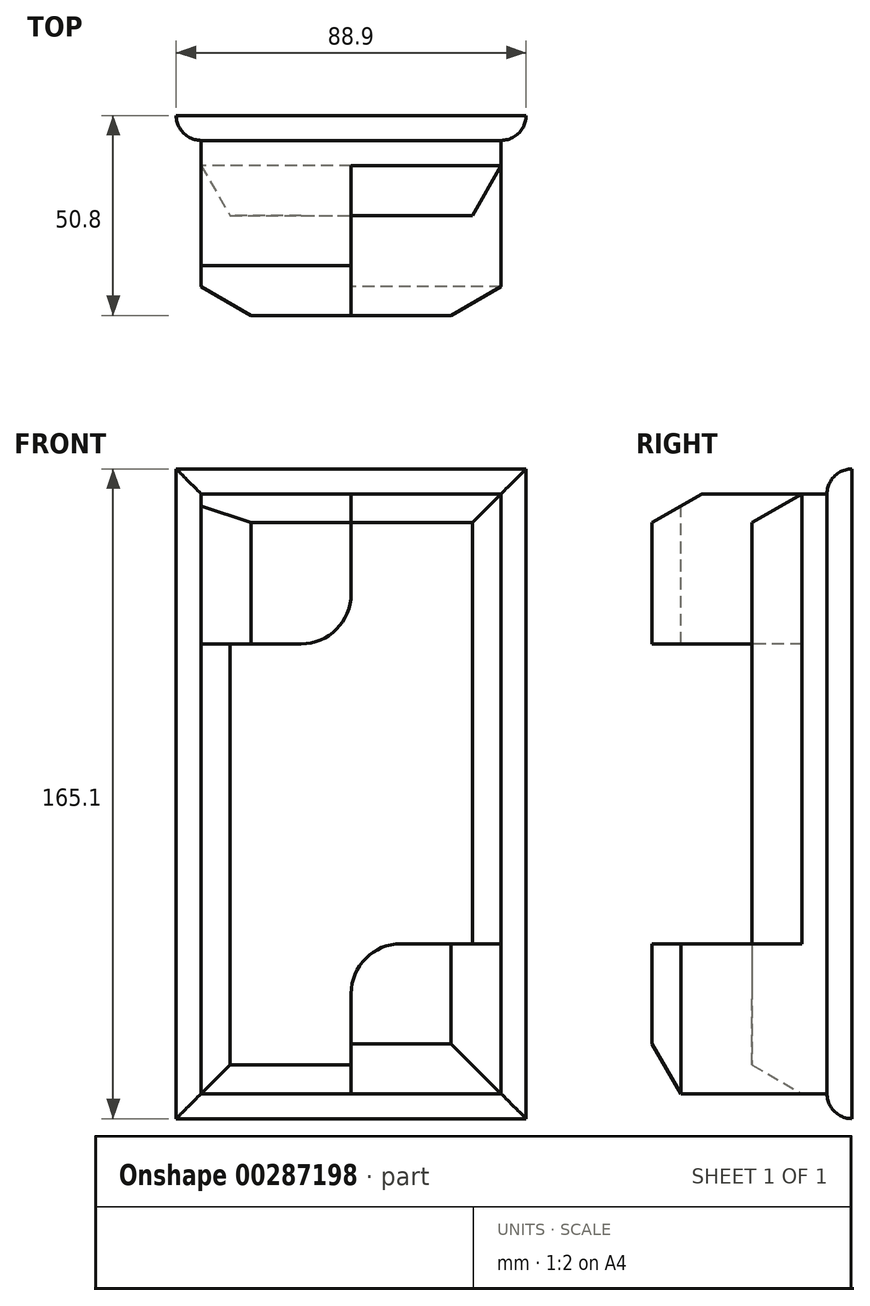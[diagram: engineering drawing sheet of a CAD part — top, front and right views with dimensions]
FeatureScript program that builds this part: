
annotation { "Feature Type Name" : "Feature", "Feature Type Description" : "" }
export const myFeature = defineFeature(function(context is Context, id is Id, definition is map)
    precondition{}
    {
        {
            var Q0;
            Q0=qCreatedBy(makeId("Front.planeOp"),FACE);
            var sketch = newSketch(context, id + "F0", { "sketchPlane" : qUnion([Q0])});
            skPoint(sketch, "E0.middle", {"position": v(0, 0) * mm});
            skLineSegment(sketch, "E1.bottom", {"start": v(-38.1, 76.2) * mm, "end": v(38.1, 76.2) * mm});
            skLineSegment(sketch, "E1.top", {"start": v(-38.1, -76.2) * mm, "end": v(38.1, -76.2) * mm});
            skLineSegment(sketch, "E1.left", {"start": v(-38.1, 76.2) * mm, "end": v(-38.1, -76.2) * mm});
            skLineSegment(sketch, "E1.right", {"start": v(38.1, 76.2) * mm, "end": v(38.1, -76.2) * mm});
            skLineSegment(sketch, "E2", {"start": v(0, 76.2) * mm, "end": v(0, 50.8) * mm});
            skLineSegment(sketch, "E3", {"start": v(-12.7, 38.1) * mm, "end": v(-38.1, 38.1) * mm});
            skLineSegment(sketch, "E4", {"start": v(0, -76.2) * mm, "end": v(0, -50.8) * mm});
            skLineSegment(sketch, "E5", {"start": v(12.7, -38.1) * mm, "end": v(38.1, -38.1) * mm});
            skPoint(sketch, "E6.visualSharp", {"position": v(0, 38.1) * mm});
            skArc(sketch, "E6.filletArc", {"start": v(-12.7, 38.1) * mm, "mid": v(-3.72, 41.82) * mm, "end": v(0, 50.8) * mm});
            skPoint(sketch, "E7.visualSharp", {"position": v(0, -38.1) * mm});
            skArc(sketch, "E7.filletArc", {"start": v(12.7, -38.1) * mm, "mid": v(3.72, -41.82) * mm, "end": v(0, -50.8) * mm});
            skLineSegment(sketch, "E8.0", {"start": v(-44.45, 82.55) * mm, "end": v(-44.45, -82.55) * mm});
            skLineSegment(sketch, "E8.1", {"start": v(-44.45, 82.55) * mm, "end": v(44.45, 82.55) * mm});
            skLineSegment(sketch, "E8.2", {"start": v(44.45, 82.55) * mm, "end": v(44.45, -82.55) * mm});
            skLineSegment(sketch, "E8.3", {"start": v(-44.45, -82.55) * mm, "end": v(44.45, -82.55) * mm});
            skSolve(sketch);
        }
        {
            var Q0;
            {var subQ9=sQuery(id+"F0.wireOp",EDGE,"E2");Q0=makeQuery(id+"F0.imprint","IMPRINT",FACE,{"disambiguationData":[TD([[makeQuery(id+"F0.imprint","IMPRINT",EDGE,{"derivedFrom":subQ9}),1.0]])]});}
            extrude(context, id + "F1", {"entities" : qUnion([Q0]), "depth" : 25.4 * mm});
        }
        {
            var Q0;
            {var subQ1=sQuery(id+"F0.wireOp",EDGE,"E4");Q0=makeQuery(id+"F0.imprint","IMPRINT",FACE,{"disambiguationData":[TD([[makeQuery(id+"F0.imprint","IMPRINT",EDGE,{"derivedFrom":subQ1}),-1.0]])]});}
            var Q1;
            {var subQ0=sQuery(id+"F0.wireOp",EDGE,"E2");Q1=makeQuery(id+"F0.imprint","IMPRINT",FACE,{"disambiguationData":[TD([[makeQuery(id+"F0.imprint","IMPRINT",EDGE,{"derivedFrom":subQ0}),-1.0]])]});}
            extrude(context, id + "F2", {"entities" : qUnion([Q0, Q1]), "operationType" : NewBodyOperationType.ADD, "depth" : 50.8 * mm});
        }
        {
            var Q0;
            Q0=makeQuery(id+"F0.imprint","IMPRINT",FACE,{"disambiguationData":[TD([[makeQuery(id+"F0.imprint","IMPRINT",EDGE,{"derivedFrom":sQuery(id+"F0.wireOp",EDGE,"E8.0")}),1.0]])]});
            extrude(context, id + "F3", {"entities" : qUnion([Q0]), "operationType" : NewBodyOperationType.ADD, "depth" : 6.35 * mm});
        }
        {
            var Q0;
            Q0=makeQuery(id+"F2.opExtrude","CAP_EDGE",EDGE,{"disambiguationData":[OSD([sQuery(id+"F0.wireOp",EDGE,"E1.top")])],"isStart":false});
            var Q1;
            Q1=makeQuery(id+"F2.opExtrude","CAP_EDGE",EDGE,{"disambiguationData":[OSD([sQuery(id+"F0.wireOp",EDGE,"E1.right")])],"isStart":false});
            var Q2;
            Q2=makeQuery(id+"F2.opExtrude","CAP_EDGE",EDGE,{"disambiguationData":[OSD([sQuery(id+"F0.wireOp",EDGE,"E1.left")])],"isStart":false});
            var Q3;
            Q3=makeQuery(id+"F2.opExtrude","CAP_EDGE",EDGE,{"disambiguationData":[OSD([sQuery(id+"F0.wireOp",EDGE,"E1.bottom")])],"isStart":false});
            chamfer(context, id + "F4", {"entities" : qUnion([Q0, Q1, Q2, Q3]), "chamferType" : ChamferType.OFFSET_ANGLE, "width" : 12.7 * mm, "oppositeDirection" : false, "angle" : 30 * degree, "tangentPropagation" : true});
        }
        {
            var Q0;
            Q0=makeQuery(id+"F1.opExtrude","CAP_EDGE",EDGE,{"disambiguationData":[OSD([sQuery(id+"F0.wireOp",EDGE,"E1.right")])],"isStart":false});
            var Q1;
            Q1=makeQuery(id+"F1.opExtrude","CAP_EDGE",EDGE,{"disambiguationData":[OSD([sQuery(id+"F0.wireOp",EDGE,"E1.bottom")])],"isStart":false});
            var Q2;
            Q2=makeQuery(id+"F1.opExtrude","CAP_EDGE",EDGE,{"disambiguationData":[OSD([sQuery(id+"F0.wireOp",EDGE,"E1.left")])],"isStart":false});
            var Q3;
            Q3=makeQuery(id+"F1.opExtrude","CAP_EDGE",EDGE,{"disambiguationData":[OSD([sQuery(id+"F0.wireOp",EDGE,"E1.top")])],"isStart":false});
            chamfer(context, id + "F5", {"entities" : qUnion([Q0, Q1, Q2, Q3]), "chamferType" : ChamferType.OFFSET_ANGLE, "width" : 12.7 * mm, "oppositeDirection" : false, "angle" : 30 * degree, "tangentPropagation" : true});
        }
        {
            var Q0;
            Q0=makeQuery(id+"F3.opExtrude","CAP_EDGE",EDGE,{"disambiguationData":[OSD([sQuery(id+"F0.wireOp",EDGE,"E8.3")])],"isStart":false});
            var Q1;
            Q1=makeQuery(id+"F3.opExtrude","CAP_EDGE",EDGE,{"disambiguationData":[OSD([sQuery(id+"F0.wireOp",EDGE,"E8.0")])],"isStart":false});
            var Q2;
            Q2=makeQuery(id+"F3.opExtrude","CAP_EDGE",EDGE,{"disambiguationData":[OSD([sQuery(id+"F0.wireOp",EDGE,"E8.1")])],"isStart":false});
            var Q3;
            Q3=makeQuery(id+"F3.opExtrude","CAP_EDGE",EDGE,{"disambiguationData":[OSD([sQuery(id+"F0.wireOp",EDGE,"E8.2")])],"isStart":false});
            fillet(context, id + "F6", {"entities" : qUnion([Q0, Q1, Q2, Q3]), "radius" : 6.35 * mm, "tangentPropagation" : true, "allowEdgeOverflow" : false});
        }
    });
